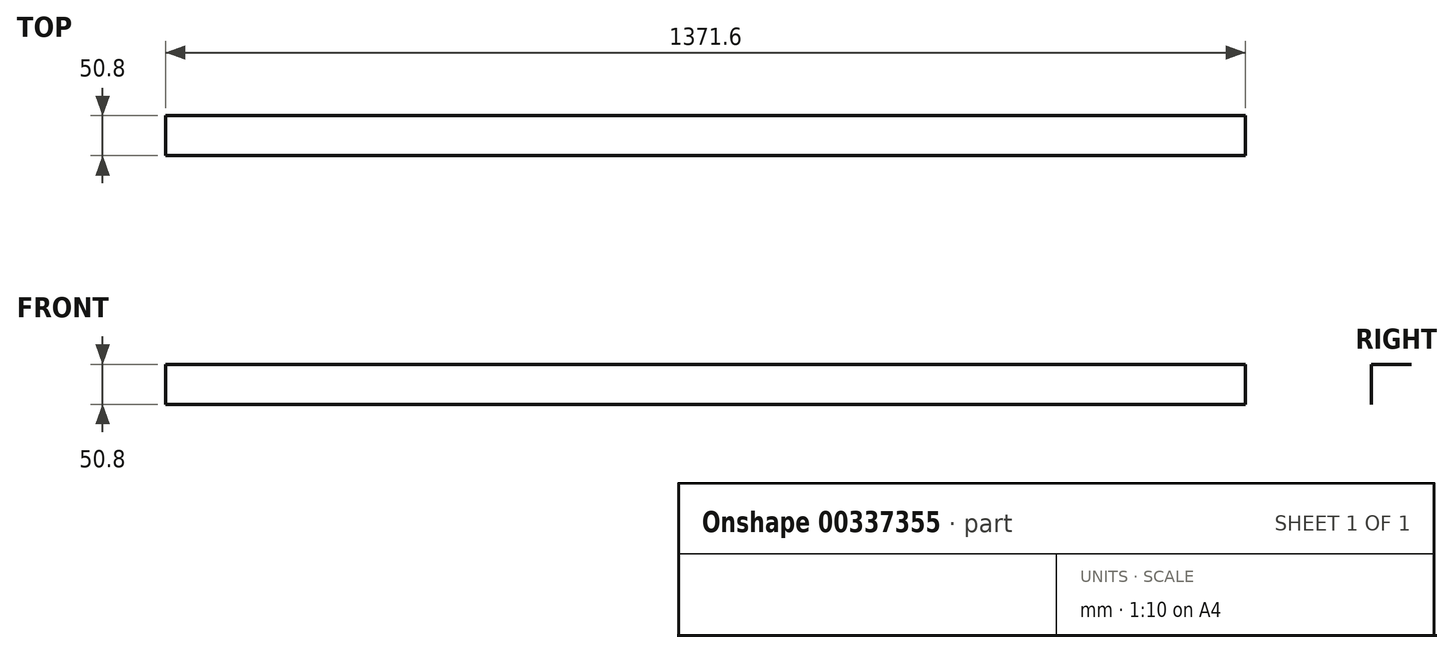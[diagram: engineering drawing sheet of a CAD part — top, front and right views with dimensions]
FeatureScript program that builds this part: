
annotation { "Feature Type Name" : "Feature", "Feature Type Description" : "" }
export const myFeature = defineFeature(function(context is Context, id is Id, definition is map)
    precondition{}
    {
        {
            var Q0;
            Q0=qCreatedBy(makeId("Right.planeOp"),FACE);
            var sketch = newSketch(context, id + "F0", { "sketchPlane" : qUnion([Q0])});
            skLineSegment(sketch, "E0", {"start": v(-64.77, -43) * mm, "end": v(-64.77, 7.8) * mm});
            skLineSegment(sketch, "E1", {"start": v(-64.77, 7.8) * mm, "end": v(-13.97, 7.8) * mm});
            skSolve(sketch);
        }
        {
            var Q0;
            Q0 = qSketchRegion(id + "F0", true);
            var Q1;
            Q1=sQuery(id+"F0.wireOp",EDGE,"E1");
            var Q2;
            Q2=sQuery(id+"F0.wireOp",EDGE,"E0");
            extrude(context, id + "F1", {"entities" : qUnion([Q0]), "bodyType" : ToolBodyType.SURFACE, "surfaceEntities" : qUnion([Q1, Q2]), "depth" : 1371.6 * mm});
        }
    });
